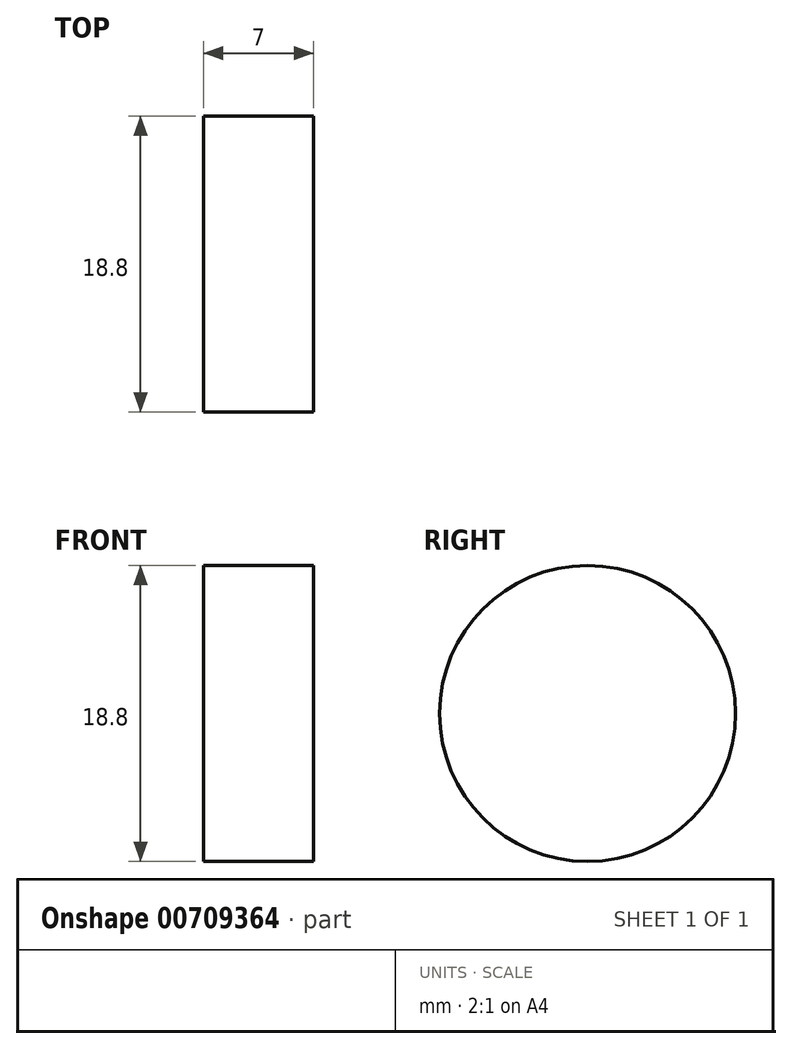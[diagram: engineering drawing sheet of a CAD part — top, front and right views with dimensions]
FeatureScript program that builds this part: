
annotation { "Feature Type Name" : "Feature", "Feature Type Description" : "" }
export const myFeature = defineFeature(function(context is Context, id is Id, definition is map)
    precondition{}
    {
        {
            var Q0;
            Q0=qCreatedBy(makeId("Right.planeOp"),FACE);
            var sketch = newSketch(context, id + "F0", { "sketchPlane" : qUnion([Q0])});
            skCircle(sketch, "E0", {"center": v(0, 0) * mm, "radius": 9.4 * mm});
            skSolve(sketch);
        }
        {
            var Q0;
            Q0 = qSketchRegion(id + "F0", true);
            extrude(context, id + "F1", {"entities" : qUnion([Q0]), "depth" : 7 * mm, "offsetDistance" : 25.4 * mm});
        }
    });
